# Revit family: revitupgrade
name_source: partatom
category: Furniture
units: mm (PartAtom-declared; Revit-internal decimal feet)

## family parameters
Always vertical = Yes
Cut with Voids When Loaded = No
Enable Cutting in Views = No
OmniClass Number = 23.40.70.14.64.11
OmniClass Title = Office Furniture
Render Appearance Source = Family Geometry
Room Calculation Point = No
Shared = No
Work Plane-Based = No

## types (4) — shared parameters
Arm and Base = Steelcase - 6205 Black
Assembly Code = E2020200
Caster = Yes
Caster/Glide = Steelcase - 6205 Black
Default Elevation = 0.00 mm
Description = A perfect fit with an exceptional range of adjustments, the Leap office chair delivers full support for various body shapes and sizes.
Glide = No
Manufacturer = Steelcase
Release Date = October 2024
URL = https://www.steelcase.com

## per-type parameters (varying)
| type | Back Frame | Iron/Control | Leg | Style Number(s) |
| Platinum Base - 3D Knit Back | Steelcase - 4799 Platinum Metallic | Steelcase - 4799 Platinum Metallic | Steelcase - 4799 Platinum Metallic | LEAP-21100, LEAP-21110,LEAP21100CN, LEAP21110CN |
| Black Base - 3D Knit Back | Steelcase - 6205 Black | Steelcase - 6205 Black | Steelcase - 6205 Black | LEAP-11100,LEAP-11110,LEAP11100CN,LEAP11110CN |
| Platinum Base - Upholstered Back | Steelcase - 4799 Platinum Metallic | Steelcase AP - J501 Ebony Omni-R | Steelcase - 4799 Platinum Metallic | LEAP-20100,LEAP-20110,LEAP20100CN,LEAP20110CN |
| Black Base - Upholstered Back | Steelcase - 6205 Black | Steelcase - 6205 Black | Steelcase - 6205 Black | LEAP-10100,LEAP-10110,LEAP10100CN,LEAP10110CN |

## geometry (parser evidence)
native form markers: Blend x4, Sweep x3
no freeform markers — native parametric forms only
